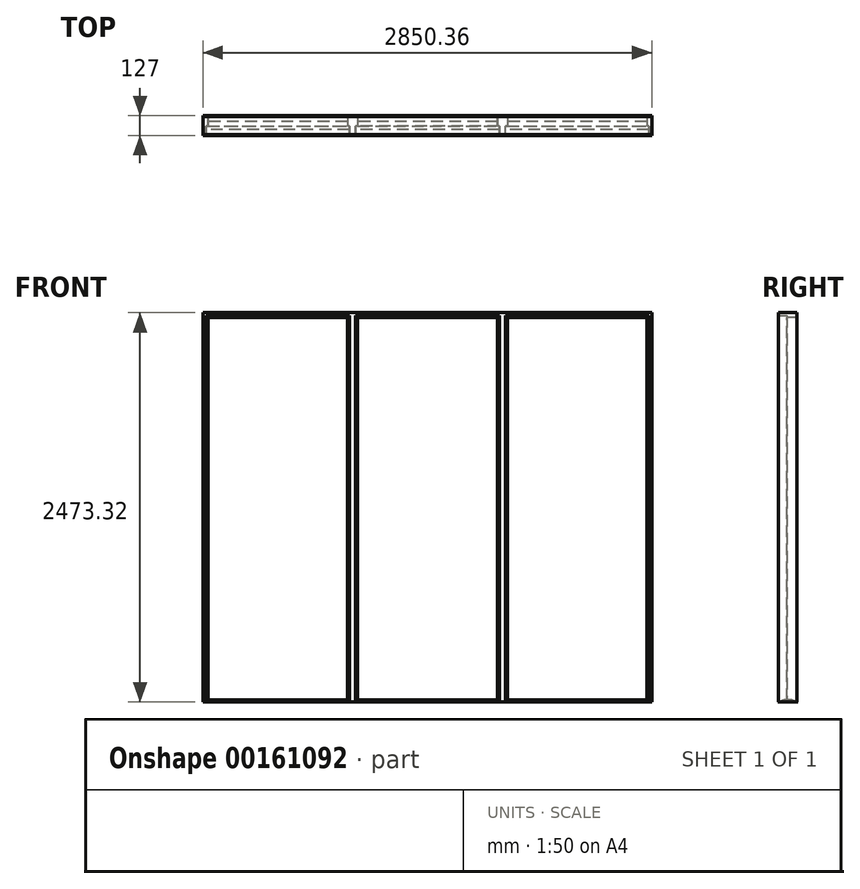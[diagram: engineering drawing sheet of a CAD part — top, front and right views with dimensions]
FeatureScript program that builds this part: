
annotation { "Feature Type Name" : "Feature", "Feature Type Description" : "" }
export const myFeature = defineFeature(function(context is Context, id is Id, definition is map)
    precondition{}
    {
        {
            var Q0;
            Q0=qCreatedBy(makeId("Front.planeOp"),FACE);
            cPlane(context, id + "F0", {"entities" : qUnion([Q0]), "cplaneType" : CPlaneType.OFFSET, "offset" : 3.17 * mm, "oppositeDirection" : true, "width" : 152.4 * mm, "height" : 152.4 * mm});
        }
        {
            var Q0;
            Q0=qCreatedBy(makeId("Front.planeOp"),FACE);
            var sketch = newSketch(context, id + "F1", { "sketchPlane" : qUnion([Q0])});
            skLineSegment(sketch, "E0.bottom", {"start": v(0, 0) * mm, "end": v(19.05, 0) * mm});
            skLineSegment(sketch, "E0.top", {"start": v(0, 2454.28) * mm, "end": v(19.05, 2454.28) * mm});
            skLineSegment(sketch, "E0.left", {"start": v(0, 0) * mm, "end": v(0, 2454.28) * mm});
            skLineSegment(sketch, "E0.right", {"start": v(19.05, 0) * mm, "end": v(19.05, 2454.28) * mm});
            skLineSegment(sketch, "E1.bottom", {"start": v(31.75, 2441.58) * mm, "end": v(19.05, 2441.58) * mm});
            skLineSegment(sketch, "E1.top", {"start": v(31.75, 0) * mm, "end": v(19.05, 0) * mm});
            skLineSegment(sketch, "E1.left", {"start": v(31.75, 2441.58) * mm, "end": v(31.75, 0) * mm});
            skLineSegment(sketch, "E1.right", {"start": v(19.05, 2441.58) * mm, "end": v(19.05, 0) * mm});
            skLineSegment(sketch, "E2.bottom", {"start": v(0, 2454.28) * mm, "end": v(2850.36, 2454.28) * mm});
            skLineSegment(sketch, "E2.top", {"start": v(0, 2473.33) * mm, "end": v(2850.36, 2473.33) * mm});
            skLineSegment(sketch, "E2.left", {"start": v(0, 2454.28) * mm, "end": v(0, 2473.33) * mm});
            skLineSegment(sketch, "E2.right", {"start": v(2850.36, 2454.28) * mm, "end": v(2850.36, 2473.33) * mm});
            skPoint(sketch, "E3.oppositeSnap0", {"position": v(9.53, 0) * mm});
            skLineSegment(sketch, "E3.bottom", {"start": v(2850.36, 2454.28) * mm, "end": v(2831.3, 2454.28) * mm});
            skLineSegment(sketch, "E3.top", {"start": v(2850.36, 0) * mm, "end": v(2831.3, 0) * mm});
            skLineSegment(sketch, "E3.left", {"start": v(2850.36, 2454.28) * mm, "end": v(2850.36, 0) * mm});
            skLineSegment(sketch, "E3.right", {"start": v(2831.3, 2454.28) * mm, "end": v(2831.3, 0) * mm});
            skLineSegment(sketch, "E4.bottom", {"start": v(2831.3, 0) * mm, "end": v(2818.6, 0) * mm});
            skLineSegment(sketch, "E4.top", {"start": v(2831.3, 2441.58) * mm, "end": v(2818.6, 2441.58) * mm});
            skLineSegment(sketch, "E4.left", {"start": v(2831.3, 0) * mm, "end": v(2831.3, 2441.58) * mm});
            skLineSegment(sketch, "E4.right", {"start": v(2818.6, 0) * mm, "end": v(2818.6, 2441.58) * mm});
            skLineSegment(sketch, "E5.bottom", {"start": v(19.05, 2454.28) * mm, "end": v(2831.3, 2454.28) * mm});
            skLineSegment(sketch, "E5.left", {"start": v(19.05, 2454.28) * mm, "end": v(19.05, 2441.58) * mm});
            skLineSegment(sketch, "E5.right", {"start": v(2831.3, 2454.28) * mm, "end": v(2831.3, 2441.58) * mm});
            skLineSegment(sketch, "E6.bottom", {"start": v(949.32, 2454.28) * mm, "end": v(930.27, 2454.28) * mm});
            skLineSegment(sketch, "E6.top", {"start": v(949.32, 0) * mm, "end": v(930.27, 0) * mm});
            skLineSegment(sketch, "E6.left", {"start": v(949.32, 2454.28) * mm, "end": v(949.32, 0) * mm});
            skLineSegment(sketch, "E6.right", {"start": v(930.27, 2454.28) * mm, "end": v(930.28, 0) * mm});
            skLineSegment(sketch, "E7.bottom", {"start": v(930.27, 0) * mm, "end": v(917.57, 0) * mm});
            skLineSegment(sketch, "E7.top", {"start": v(930.27, 2441.58) * mm, "end": v(917.57, 2441.58) * mm});
            skLineSegment(sketch, "E7.left", {"start": v(930.27, 0) * mm, "end": v(930.27, 2441.58) * mm});
            skLineSegment(sketch, "E7.right", {"start": v(917.57, 0) * mm, "end": v(917.57, 2441.58) * mm});
            skLineSegment(sketch, "E8.bottom", {"start": v(949.32, 2454.28) * mm, "end": v(968.38, 2454.28) * mm});
            skLineSegment(sketch, "E8.top", {"start": v(949.32, 0) * mm, "end": v(968.38, 0) * mm});
            skLineSegment(sketch, "E8.right", {"start": v(968.37, 2454.28) * mm, "end": v(968.38, 0) * mm});
            skLineSegment(sketch, "E9.bottom", {"start": v(968.38, 0) * mm, "end": v(981.08, 0) * mm});
            skLineSegment(sketch, "E9.top", {"start": v(968.37, 2441.58) * mm, "end": v(981.07, 2441.58) * mm});
            skLineSegment(sketch, "E9.left", {"start": v(968.38, 0) * mm, "end": v(968.37, 2441.58) * mm});
            skLineSegment(sketch, "E9.right", {"start": v(981.08, 0) * mm, "end": v(981.07, 2441.58) * mm});
            skLineSegment(sketch, "E10.bottom", {"start": v(1901.03, 2454.28) * mm, "end": v(1881.98, 2454.28) * mm});
            skLineSegment(sketch, "E10.top", {"start": v(1901.03, 0) * mm, "end": v(1881.98, 0) * mm});
            skLineSegment(sketch, "E10.left", {"start": v(1901.03, 2454.28) * mm, "end": v(1901.03, 0) * mm});
            skLineSegment(sketch, "E10.right", {"start": v(1881.98, 2454.28) * mm, "end": v(1881.98, 0) * mm});
            skLineSegment(sketch, "E11.bottom", {"start": v(1901.03, 0) * mm, "end": v(1920.08, 0) * mm});
            skLineSegment(sketch, "E11.top", {"start": v(1901.03, 2454.28) * mm, "end": v(1920.08, 2454.28) * mm});
            skLineSegment(sketch, "E11.left", {"start": v(1901.03, 0) * mm, "end": v(1901.03, 2454.28) * mm});
            skLineSegment(sketch, "E11.right", {"start": v(1920.08, 0) * mm, "end": v(1920.08, 2454.28) * mm});
            skLineSegment(sketch, "E12.bottom", {"start": v(1881.98, 2441.58) * mm, "end": v(1869.28, 2441.58) * mm});
            skLineSegment(sketch, "E12.top", {"start": v(1881.98, 0) * mm, "end": v(1869.28, 0) * mm});
            skLineSegment(sketch, "E12.left", {"start": v(1881.98, 2441.58) * mm, "end": v(1881.98, 0) * mm});
            skLineSegment(sketch, "E12.right", {"start": v(1869.28, 2441.58) * mm, "end": v(1869.28, 0) * mm});
            skLineSegment(sketch, "E13.bottom", {"start": v(1920.08, 0) * mm, "end": v(1932.78, 0) * mm});
            skLineSegment(sketch, "E13.top", {"start": v(1920.08, 2441.58) * mm, "end": v(1932.78, 2441.58) * mm});
            skLineSegment(sketch, "E13.left", {"start": v(1920.08, 0) * mm, "end": v(1920.08, 2441.58) * mm});
            skLineSegment(sketch, "E13.right", {"start": v(1932.78, 0) * mm, "end": v(1932.78, 2441.58) * mm});
            skLineSegment(sketch, "E14.bottom", {"start": v(19.05, 2454.28) * mm, "end": v(930.27, 2454.28) * mm});
            skLineSegment(sketch, "E14.top", {"start": v(19.05, 2441.58) * mm, "end": v(930.27, 2441.58) * mm});
            skLineSegment(sketch, "E14.right", {"start": v(930.27, 2454.28) * mm, "end": v(930.27, 2441.58) * mm});
            skLineSegment(sketch, "E15.bottom", {"start": v(968.38, 2454.28) * mm, "end": v(1881.98, 2454.28) * mm});
            skLineSegment(sketch, "E15.top", {"start": v(968.37, 2441.58) * mm, "end": v(1881.98, 2441.58) * mm});
            skLineSegment(sketch, "E15.left", {"start": v(968.37, 2454.28) * mm, "end": v(968.37, 2441.58) * mm});
            skLineSegment(sketch, "E15.right", {"start": v(1881.98, 2454.28) * mm, "end": v(1881.98, 2441.58) * mm});
            skLineSegment(sketch, "E16.bottom", {"start": v(1920.08, 2454.28) * mm, "end": v(2831.3, 2454.28) * mm});
            skLineSegment(sketch, "E16.top", {"start": v(1920.08, 2441.58) * mm, "end": v(2831.3, 2441.58) * mm});
            skLineSegment(sketch, "E16.left", {"start": v(1920.08, 2454.28) * mm, "end": v(1920.08, 2441.58) * mm});
            skSolve(sketch);
        }
        {
            var Q0;
            Q0=qCreatedBy(id+"F0.planeOp",FACE);
            var sketch = newSketch(context, id + "F2", { "sketchPlane" : qUnion([Q0])});
            skLineSegment(sketch, "E17.0", {"start": v(0, 0) * mm, "end": v(0, 2454.28) * mm});
            skLineSegment(sketch, "E18.0", {"start": v(0, 0) * mm, "end": v(19.05, 0) * mm});
            skLineSegment(sketch, "E19.0", {"start": v(31.75, 0) * mm, "end": v(19.05, 0) * mm});
            skLineSegment(sketch, "E20.0", {"start": v(31.75, 2441.58) * mm, "end": v(31.75, 0) * mm});
            skLineSegment(sketch, "E21.0", {"start": v(19.05, 2441.58) * mm, "end": v(930.27, 2441.58) * mm});
            skLineSegment(sketch, "E22.0", {"start": v(917.57, 0) * mm, "end": v(917.57, 2441.58) * mm});
            skLineSegment(sketch, "E23.0", {"start": v(0, 2473.33) * mm, "end": v(2850.36, 2473.33) * mm});
            skLineSegment(sketch, "E24.0", {"start": v(0, 2454.28) * mm, "end": v(0, 2473.33) * mm});
            skLineSegment(sketch, "E25.0", {"start": v(968.37, 2441.58) * mm, "end": v(1881.98, 2441.58) * mm});
            skLineSegment(sketch, "E26.0", {"start": v(981.08, 0) * mm, "end": v(981.07, 2441.58) * mm});
            skLineSegment(sketch, "E27.0", {"start": v(1869.28, 2441.58) * mm, "end": v(1869.28, 0) * mm});
            skLineSegment(sketch, "E28.0", {"start": v(1932.78, 0) * mm, "end": v(1932.78, 2441.58) * mm});
            skLineSegment(sketch, "E29.0", {"start": v(1920.08, 2441.58) * mm, "end": v(2831.3, 2441.58) * mm});
            skLineSegment(sketch, "E30.0", {"start": v(2818.6, 0) * mm, "end": v(2818.6, 2441.58) * mm});
            skLineSegment(sketch, "E31.0", {"start": v(2850.36, 2454.28) * mm, "end": v(2850.36, 0) * mm});
            skLineSegment(sketch, "E32.0", {"start": v(2850.36, 2454.28) * mm, "end": v(2850.36, 2473.33) * mm});
            skLineSegment(sketch, "E33.0", {"start": v(930.27, 0) * mm, "end": v(917.57, 0) * mm});
            skLineSegment(sketch, "E34.0", {"start": v(949.32, 0) * mm, "end": v(930.27, 0) * mm});
            skLineSegment(sketch, "E35.0", {"start": v(949.32, 0) * mm, "end": v(968.38, 0) * mm});
            skLineSegment(sketch, "E36.0", {"start": v(968.38, 0) * mm, "end": v(981.08, 0) * mm});
            skLineSegment(sketch, "E37.0", {"start": v(1881.98, 0) * mm, "end": v(1869.28, 0) * mm});
            skLineSegment(sketch, "E38.0", {"start": v(1901.03, 0) * mm, "end": v(1881.98, 0) * mm});
            skLineSegment(sketch, "E39.0", {"start": v(1901.03, 0) * mm, "end": v(1920.08, 0) * mm});
            skLineSegment(sketch, "E40.0", {"start": v(1920.08, 0) * mm, "end": v(1932.78, 0) * mm});
            skLineSegment(sketch, "E41.0", {"start": v(2831.3, 0) * mm, "end": v(2818.6, 0) * mm});
            skLineSegment(sketch, "E42.0", {"start": v(2850.36, 0) * mm, "end": v(2831.3, 0) * mm});
            skSolve(sketch);
        }
        {
            var Q0;
            Q0=qSketchRegion(id+"F2",true);
            extrude(context, id + "F3", {"entities" : qUnion([Q0]), "oppositeDirection" : true, "depth" : 61.9 * mm});
        }
        {
            var Q0;
            Q0=qCreatedBy(makeId("Front.planeOp"),FACE);
            var sketch = newSketch(context, id + "F4", { "sketchPlane" : qUnion([Q0])});
            skLineSegment(sketch, "E43.0", {"start": v(0, 0) * mm, "end": v(19.05, 0) * mm});
            skLineSegment(sketch, "E44.0", {"start": v(19.05, 2441.58) * mm, "end": v(19.05, 0) * mm});
            skLineSegment(sketch, "E45.0", {"start": v(0, 0) * mm, "end": v(0, 2454.28) * mm});
            skLineSegment(sketch, "E46.0", {"start": v(0, 2454.28) * mm, "end": v(0, 2473.33) * mm});
            skLineSegment(sketch, "E47.0", {"start": v(0, 2473.33) * mm, "end": v(2850.36, 2473.33) * mm});
            skLineSegment(sketch, "E48.0", {"start": v(19.05, 2454.28) * mm, "end": v(19.05, 2441.58) * mm});
            skLineSegment(sketch, "E49.0", {"start": v(19.05, 2454.28) * mm, "end": v(930.27, 2454.28) * mm});
            skLineSegment(sketch, "E50.0", {"start": v(930.27, 2454.28) * mm, "end": v(930.28, 0) * mm});
            skLineSegment(sketch, "E51.0", {"start": v(968.37, 2454.28) * mm, "end": v(968.38, 0) * mm});
            skLineSegment(sketch, "E52.0", {"start": v(949.32, 0) * mm, "end": v(930.27, 0) * mm});
            skLineSegment(sketch, "E53.0", {"start": v(949.32, 0) * mm, "end": v(968.38, 0) * mm});
            skLineSegment(sketch, "E54.0", {"start": v(1881.98, 2454.28) * mm, "end": v(1881.98, 2441.58) * mm});
            skLineSegment(sketch, "E55.0", {"start": v(1881.98, 2441.58) * mm, "end": v(1881.98, 0) * mm});
            skLineSegment(sketch, "E56.0", {"start": v(1920.08, 2454.28) * mm, "end": v(1920.08, 2441.58) * mm});
            skLineSegment(sketch, "E57.0", {"start": v(1920.08, 0) * mm, "end": v(1920.08, 2441.58) * mm});
            skLineSegment(sketch, "E58.0", {"start": v(2831.3, 2454.28) * mm, "end": v(2831.3, 2441.58) * mm});
            skLineSegment(sketch, "E59.0", {"start": v(2831.3, 0) * mm, "end": v(2831.3, 2441.58) * mm});
            skLineSegment(sketch, "E60.0", {"start": v(2850.36, 2454.28) * mm, "end": v(2850.36, 0) * mm});
            skPoint(sketch, "E61.0", {"position": v(2850.36, 2463.8) * mm});
            skLineSegment(sketch, "E62.0", {"start": v(2850.36, 2454.28) * mm, "end": v(2850.36, 2473.33) * mm});
            skLineSegment(sketch, "E63", {"start": v(1920.08, 2454.28) * mm, "end": v(2831.3, 2454.28) * mm});
            skLineSegment(sketch, "E64", {"start": v(1881.98, 2454.28) * mm, "end": v(968.37, 2454.28) * mm});
            skLineSegment(sketch, "E65.0", {"start": v(1901.03, 0) * mm, "end": v(1881.98, 0) * mm});
            skLineSegment(sketch, "E66.0", {"start": v(1901.03, 0) * mm, "end": v(1920.08, 0) * mm});
            skLineSegment(sketch, "E67.0", {"start": v(2850.36, 0) * mm, "end": v(2831.3, 0) * mm});
            skSolve(sketch);
        }
        {
            var Q0;
            Q0=qSketchRegion(id+"F4",true);
            extrude(context, id + "F5", {"entities" : qUnion([Q0]), "operationType" : NewBodyOperationType.ADD, "depth" : 50.8 * mm, "hasSecondDirection" : true, "secondDirectionOppositeDirection" : true, "secondDirectionDepth" : 3.17 * mm});
        }
        {
            var Q0;
            Q0=qCreatedBy(makeId("Right.planeOp"),FACE);
            var sketch = newSketch(context, id + "F6", { "sketchPlane" : qUnion([Q0])});
            skLineSegment(sketch, "E68.0", {"start": v(65.09, 0) * mm, "end": v(-50.8, 0) * mm});
            skLineSegment(sketch, "E69", {"start": v(7.14, 0) * mm, "end": v(70.64, 0) * mm});
            skLineSegment(sketch, "E70", {"start": v(7.14, 0) * mm, "end": v(-56.36, 0) * mm});
            skLineSegment(sketch, "E71", {"start": v(-18.26, 12.7) * mm, "end": v(32.54, 12.7) * mm});
            skLineSegment(sketch, "E72", {"start": v(-56.36, 0) * mm, "end": v(-18.26, 12.7) * mm});
            skLineSegment(sketch, "E73", {"start": v(32.54, 12.7) * mm, "end": v(70.64, 0) * mm});
            skSolve(sketch);
        }
        {
            var Q0;
            Q0 = qSketchRegion(id + "F6", true);
            var Q1;
            Q1=makeQuery(id+"F5.boolean.opBoolean","MERGE",FACE,{"derivedFrom":[makeQuery(id+"F3.opExtrude","SWEPT_FACE",FACE,{"disambiguationData":[OSD([sQuery(id+"F2.wireOp",EDGE,"E31.0"),sQuery(id+"F2.wireOp",EDGE,"E32.0")])]}),makeQuery(id+"F5.opExtrude","SWEPT_FACE",FACE,{"disambiguationData":[OSD([sQuery(id+"F4.wireOp",EDGE,"E60.0"),sQuery(id+"F4.wireOp",EDGE,"E62.0")])]})]});
            extrude(context, id + "F7", {"entities" : qUnion([Q0]), "operationType" : NewBodyOperationType.ADD, "endBound" : BoundingType.UP_TO_SURFACE, "endBoundEntityFace" : qUnion([Q1]), "depth" : 25.4 * mm});
        }
    });
